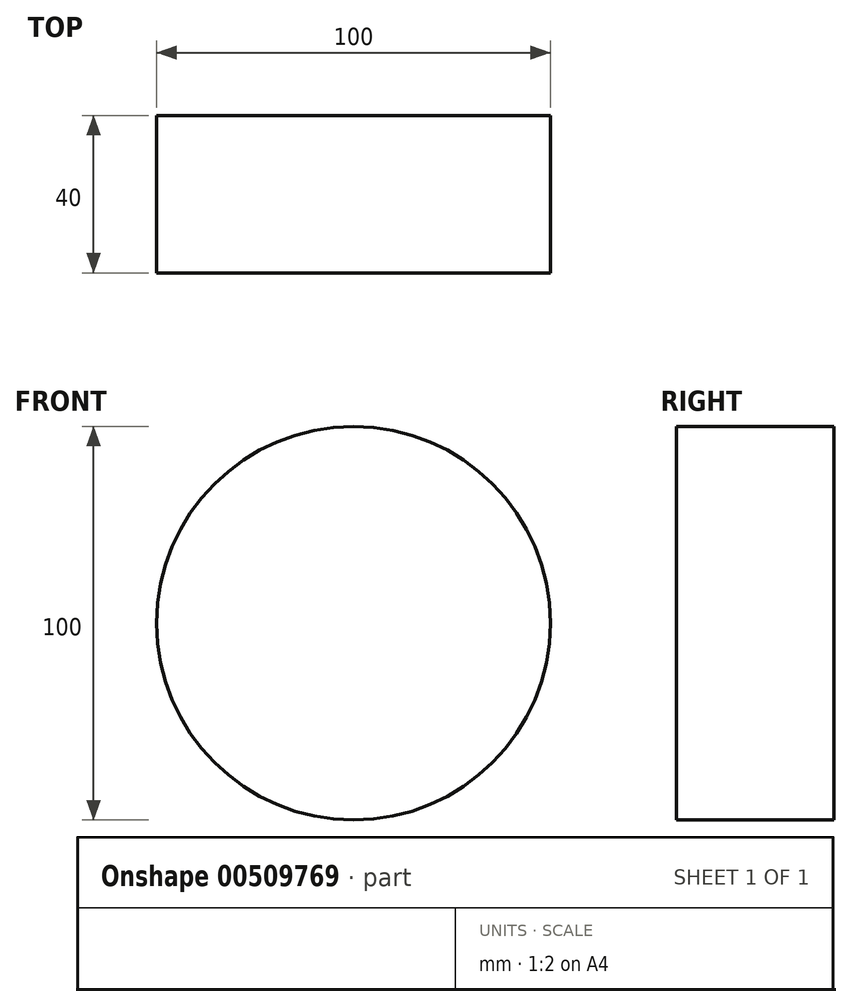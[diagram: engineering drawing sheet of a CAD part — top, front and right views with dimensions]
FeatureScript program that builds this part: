
annotation { "Feature Type Name" : "Feature", "Feature Type Description" : "" }
export const myFeature = defineFeature(function(context is Context, id is Id, definition is map)
    precondition{}
    {
        {
            var Q0;
            Q0=qCreatedBy(makeId("Front.planeOp"),FACE);
            var sketch = newSketch(context, id + "F0", { "sketchPlane" : qUnion([Q0])});
            skCircle(sketch, "E0", {"center": v(0, 0) * mm, "radius": 50 * mm});
            skSolve(sketch);
        }
        {
            var Q0;
            Q0 = qSketchRegion(id + "F0", true);
            extrude(context, id + "F1", {"entities" : qUnion([Q0]), "depth" : 40 * mm});
        }
    });
